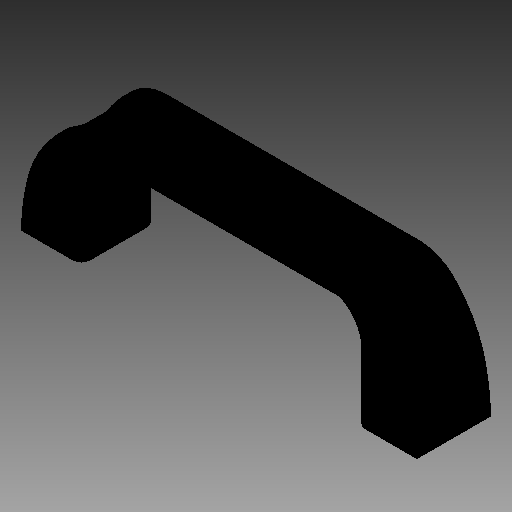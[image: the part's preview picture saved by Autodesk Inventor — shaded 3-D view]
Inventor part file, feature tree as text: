
AUTODESK INVENTOR PART (.ipt)
format: ipt  version: 2019 (Build 230136000, 136)  size: 214,528 bytes
history: native  units: in
note: dims shown in document units (in); Inventor stores cm internally (conversion verified against a paired STEP export)
features: sketch x9, extrude x5, revolve x4
ambient origin geometry x8: Origin, YZ Plane, XZ Plane, XY Plane, X Axis, Y Axis, Z Axis, Center Point
bodies: Solid1 (feature_tree)
feature tree (18):
  extrude  "Extrusion1"  Depth=5.473in TaperAngle=0.0deg
  extrude  "Extrusion2"  TaperAngle=90.0deg  [1 undecoded]
  extrude  "Extrusion3"  Depth=2.048in TaperAngle=0.0deg
  revolve  "Revolution1"  Angle=360.0deg
  revolve  "Revolution2"  [1 undecoded]
  extrude  "Extrusion4"  [1 undecoded]
  revolve  "Revolution3"  [1 undecoded]
  revolve  "Revolution4"  [1 undecoded]
  extrude  "Extrusion5"  [1 undecoded]
  sketch  "Sketch_10"  dims[d0=1.614in d1=0.0in d2=5.473in d3=0.0in]
  sketch  "Sketch_11"  dims[d4=1.614in d5=0.0in d6=90.0deg]
  sketch  "Sketch_12"  dims[d7=90.0deg d8=2.048in d9=0.0in]
  sketch  "Sketch_13"  dims[d10=360.0deg d11=360.0deg]
  sketch  "Sketch_14"  dims[d12=1.0238in d13=0.0in]
  sketch  "Sketch_15"
  sketch  "Sketch_16"
  sketch  "Sketch_17"
  sketch  "Sketch_18"
note: 6 required parameter values undecoded (feature->parameter linkage not recoverable at this tier; creation-order binding heuristic only, values carry confidence <= 0.55)
